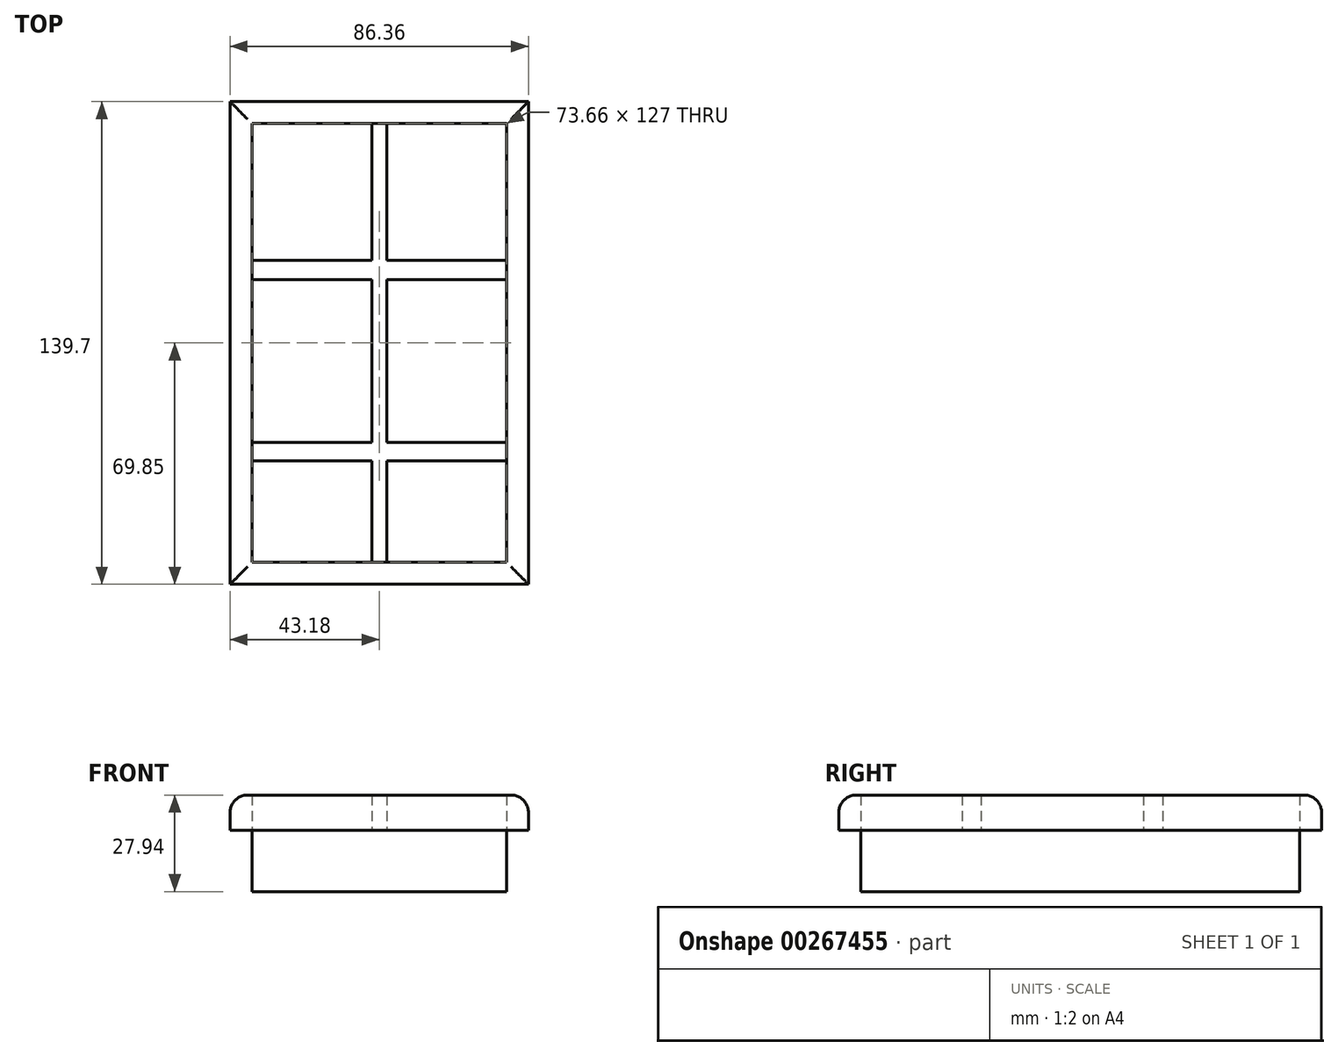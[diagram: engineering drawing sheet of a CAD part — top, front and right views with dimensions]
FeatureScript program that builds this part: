
annotation { "Feature Type Name" : "Feature", "Feature Type Description" : "" }
export const myFeature = defineFeature(function(context is Context, id is Id, definition is map)
    precondition{}
    {
        {
            var Q0;
            Q0=qCreatedBy(makeId("Top.planeOp"),FACE);
            var sketch = newSketch(context, id + "F0", { "sketchPlane" : qUnion([Q0])});
            skLineSegment(sketch, "E0.bottom", {"start": v(-43.18, 69.85) * mm, "end": v(43.18, 69.85) * mm});
            skLineSegment(sketch, "E0.top", {"start": v(-43.18, -69.85) * mm, "end": v(43.18, -69.85) * mm});
            skLineSegment(sketch, "E0.left", {"start": v(-43.18, 69.85) * mm, "end": v(-43.18, -69.85) * mm});
            skLineSegment(sketch, "E0.right", {"start": v(43.18, 69.85) * mm, "end": v(43.18, -69.85) * mm});
            skPoint(sketch, "E0.middle", {"position": v(0, 0) * mm});
            skLineSegment(sketch, "E1.bottom", {"start": v(-36.83, -63.5) * mm, "end": v(36.83, -63.5) * mm});
            skLineSegment(sketch, "E1.top", {"start": v(-36.83, 63.5) * mm, "end": v(36.83, 63.5) * mm});
            skLineSegment(sketch, "E1.left", {"start": v(-36.83, -63.5) * mm, "end": v(-36.83, 63.5) * mm});
            skLineSegment(sketch, "E1.right", {"start": v(36.83, -63.5) * mm, "end": v(36.83, 63.5) * mm});
            skSolve(sketch);
        }
        {
            var Q0;
            Q0 = qSketchRegion(id + "F0", true);
            extrude(context, id + "F1", {"entities" : qUnion([Q0]), "depth" : 10.16 * mm});
        }
        {
            var Q0;
            Q0=makeQuery(id+"F0.imprint","IMPRINT",FACE,{"disambiguationData":[TD([[makeQuery(id+"F0.imprint","IMPRINT",EDGE,{"derivedFrom":sQuery(id+"F0.wireOp",EDGE,"E1.bottom")}),1.0]])]});
            extrude(context, id + "F2", {"entities" : qUnion([Q0]), "operationType" : NewBodyOperationType.ADD, "oppositeDirection" : true, "depth" : 17.78 * mm});
        }
        {
            var Q0;
            Q0=makeQuery(id+"F1.opExtrude","CAP_EDGE",EDGE,{"disambiguationData":[OSD([sQuery(id+"F0.wireOp",EDGE,"E0.left")])],"isStart":false});
            var Q1;
            Q1=makeQuery(id+"F1.opExtrude","CAP_EDGE",EDGE,{"disambiguationData":[OSD([sQuery(id+"F0.wireOp",EDGE,"E0.bottom")])],"isStart":false});
            var Q2;
            Q2=makeQuery(id+"F1.opExtrude","CAP_EDGE",EDGE,{"disambiguationData":[OSD([sQuery(id+"F0.wireOp",EDGE,"E0.right")])],"isStart":false});
            var Q3;
            Q3=makeQuery(id+"F1.opExtrude","CAP_EDGE",EDGE,{"disambiguationData":[OSD([sQuery(id+"F0.wireOp",EDGE,"E0.top")])],"isStart":false});
            fillet(context, id + "F3", {"entities" : qUnion([Q0, Q1, Q2, Q3]), "radius" : 5.08 * mm, "tangentPropagation" : true, "allowEdgeOverflow" : false});
        }
        {
            var Q0;
            Q0=makeQuery(id+"F2.opExtrude","CAP_FACE",FACE,{"disambiguationData":[OSD([sQuery(id+"F0.wireOp",EDGE,"E1.bottom"),sQuery(id+"F0.wireOp",EDGE,"E1.top"),sQuery(id+"F0.wireOp",EDGE,"E1.left"),sQuery(id+"F0.wireOp",EDGE,"E1.right")])],"isStart":true});
            var sketch = newSketch(context, id + "F4", { "sketchPlane" : qUnion([Q0])});
            skLineSegment(sketch, "E2.bottom", {"start": v(-2.17, 63.5) * mm, "end": v(2.17, 63.5) * mm});
            skLineSegment(sketch, "E2.top", {"start": v(-2.17, -63.5) * mm, "end": v(2.17, -63.5) * mm});
            skLineSegment(sketch, "E2.left", {"start": v(-2.17, 63.5) * mm, "end": v(-2.17, -63.5) * mm});
            skLineSegment(sketch, "E2.right", {"start": v(2.17, 63.5) * mm, "end": v(2.17, -63.5) * mm});
            skPoint(sketch, "E2.middle", {"position": v(0, 0) * mm});
            skLineSegment(sketch, "E3.bottom", {"start": v(36.83, -34.11) * mm, "end": v(-36.83, -34.11) * mm});
            skLineSegment(sketch, "E3.top", {"start": v(36.83, -28.73) * mm, "end": v(-36.83, -28.73) * mm});
            skLineSegment(sketch, "E3.left", {"start": v(36.83, -34.11) * mm, "end": v(36.83, -28.73) * mm});
            skLineSegment(sketch, "E3.right", {"start": v(-36.83, -34.11) * mm, "end": v(-36.83, -28.73) * mm});
            skLineSegment(sketch, "E4.bottom", {"start": v(36.83, 23.86) * mm, "end": v(-36.83, 23.86) * mm});
            skLineSegment(sketch, "E4.top", {"start": v(36.83, 18.27) * mm, "end": v(-36.83, 18.27) * mm});
            skLineSegment(sketch, "E4.left", {"start": v(36.83, 23.86) * mm, "end": v(36.83, 18.27) * mm});
            skLineSegment(sketch, "E4.right", {"start": v(-36.83, 23.86) * mm, "end": v(-36.83, 18.27) * mm});
            skSolve(sketch);
        }
        {
            var Q0;
            Q0 = qSketchRegion(id + "F4", true);
            extrude(context, id + "F5", {"entities" : qUnion([Q0]), "depth" : 10.16 * mm});
        }
    });
